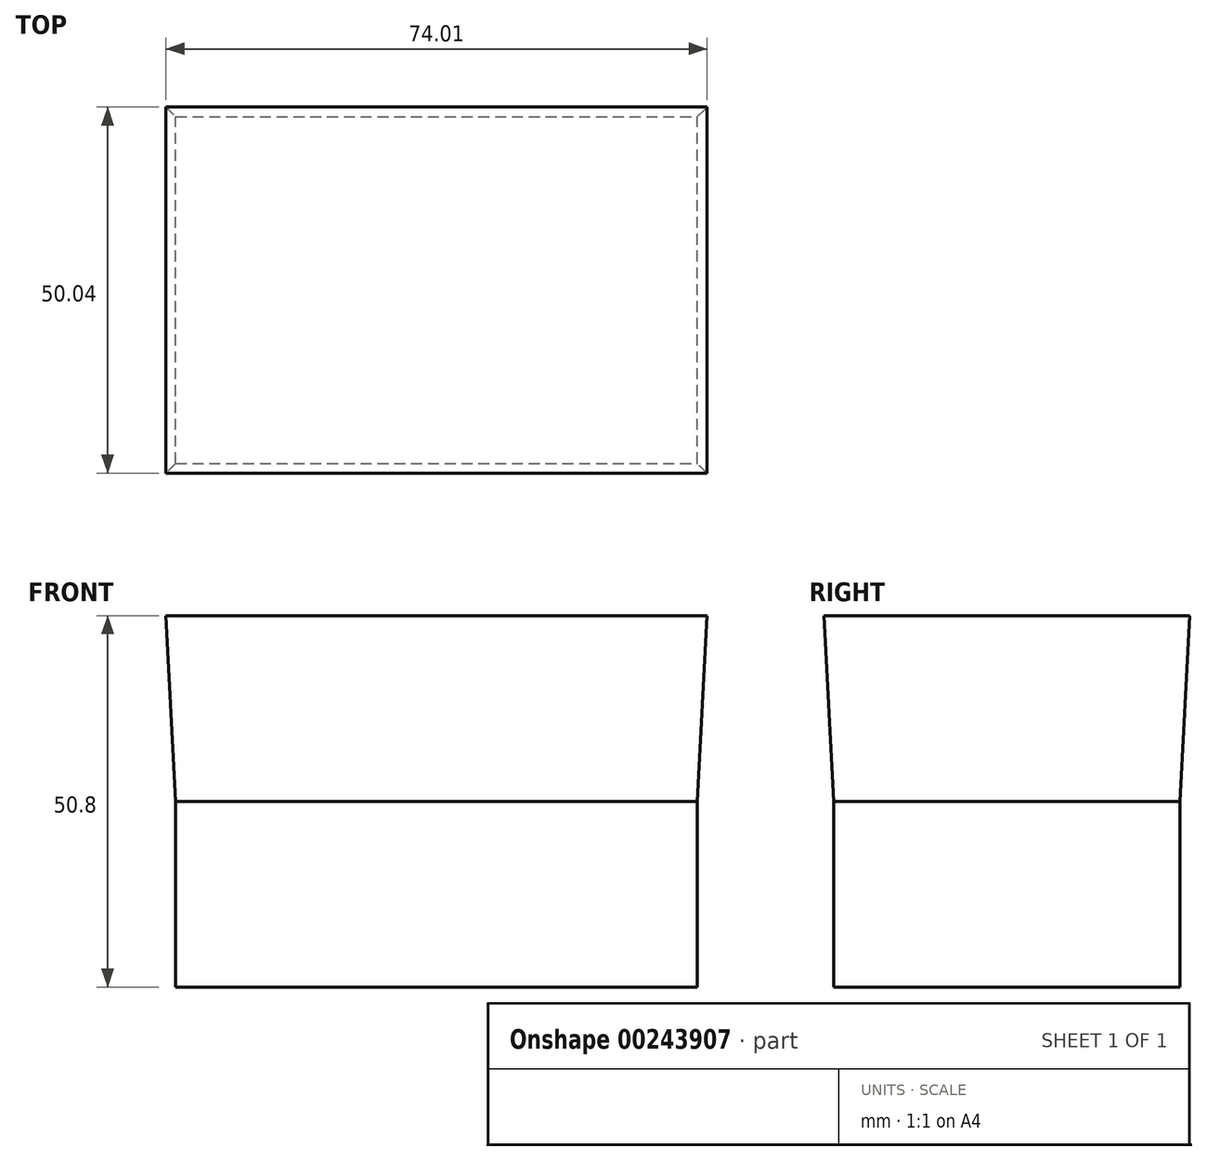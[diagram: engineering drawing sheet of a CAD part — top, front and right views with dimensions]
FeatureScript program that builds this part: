
annotation { "Feature Type Name" : "Feature", "Feature Type Description" : "" }
export const myFeature = defineFeature(function(context is Context, id is Id, definition is map)
    precondition{}
    {
        {
            var Q0;
            Q0=qCreatedBy(makeId("Top.planeOp"),FACE);
            var sketch = newSketch(context, id + "F0", { "sketchPlane" : qUnion([Q0])});
            skLineSegment(sketch, "E0.bottom", {"start": v(0, 0) * mm, "end": v(71.35, 0) * mm});
            skLineSegment(sketch, "E0.top", {"start": v(0, 47.38) * mm, "end": v(71.35, 47.38) * mm});
            skLineSegment(sketch, "E0.left", {"start": v(0, 0) * mm, "end": v(0, 47.38) * mm});
            skLineSegment(sketch, "E0.right", {"start": v(71.35, 0) * mm, "end": v(71.35, 47.38) * mm});
            skSolve(sketch);
        }
        {
            var Q0;
            Q0=makeQuery(id+"F0.imprint","IMPRINT",FACE,{"disambiguationData":[TD([[makeQuery(id+"F0.imprint","IMPRINT",EDGE,{"derivedFrom":sQuery(id+"F0.wireOp",EDGE,"E0.bottom")}),1.0]])]});
            extrude(context, id + "F1", {"entities" : qUnion([Q0]), "depth" : 25.4 * mm, "hasDraft" : true, "draftAngle" : 3 * degree, "hasSecondDirection" : true, "secondDirectionOppositeDirection" : true, "secondDirectionDepth" : 25.4 * mm});
        }
    });
